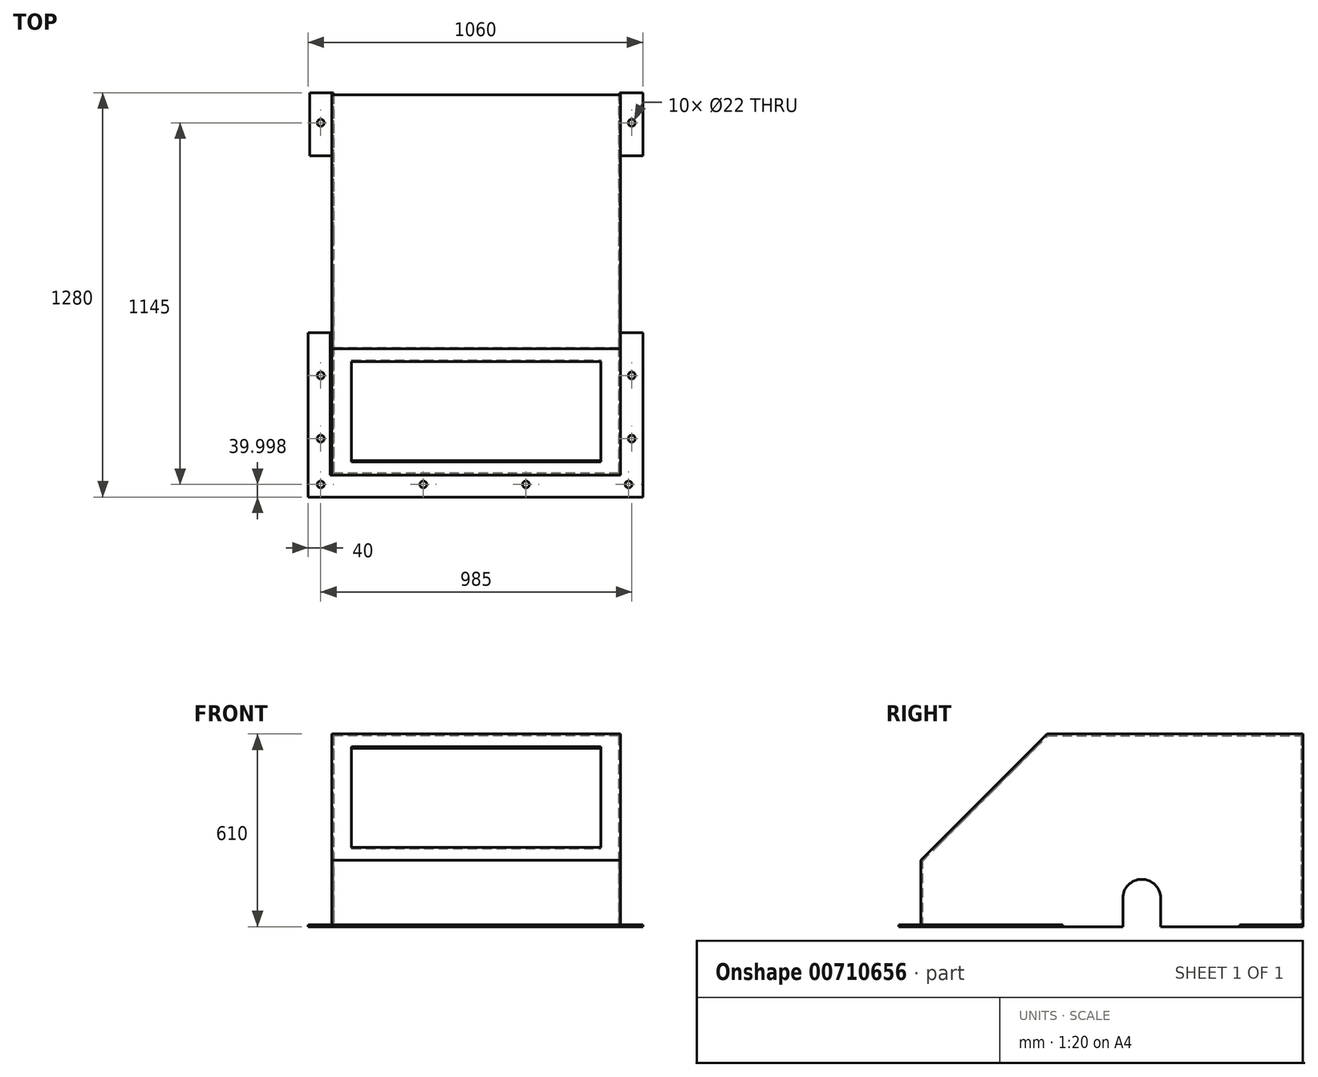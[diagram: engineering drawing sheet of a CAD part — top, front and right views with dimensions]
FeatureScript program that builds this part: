
annotation { "Feature Type Name" : "Feature", "Feature Type Description" : "" }
export const myFeature = defineFeature(function(context is Context, id is Id, definition is map)
    precondition{}
    {
        {
            var Q0;
            Q0=qCreatedBy(makeId("Right.planeOp"),FACE);
            var sketch = newSketch(context, id + "F0", { "sketchPlane" : qUnion([Q0])});
            skLineSegment(sketch, "E0", {"start": v(1114.84, 0) * mm, "end": v(-95.16, 0) * mm});
            skLineSegment(sketch, "E1", {"start": v(-95.16, 0) * mm, "end": v(-95.16, 210) * mm});
            skLineSegment(sketch, "E2", {"start": v(-95.16, 210) * mm, "end": v(304.84, 610) * mm});
            skLineSegment(sketch, "E3", {"start": v(304.84, 610) * mm, "end": v(1114.84, 610) * mm});
            skLineSegment(sketch, "E4", {"start": v(1114.84, 610) * mm, "end": v(1114.84, 0) * mm});
            skSolve(sketch);
        }
        {
            var Q0;
            Q0 = qSketchRegion(id + "F0", true);
            extrude(context, id + "F1", {"entities" : qUnion([Q0]), "endBound" : BoundingType.SYMMETRIC, "depth" : 915 * mm, "offsetDistance" : 25 * mm});
        }
        {
            var Q0;
            Q0=makeQuery(id+"F1.opExtrude","SWEPT_FACE",FACE,{"disambiguationData":[OSD([sQuery(id+"F0.wireOp",EDGE,"E0")])]});
            shell(context, id + "F2", {"entities" : qUnion([Q0]), "thickness" : 6 * mm});
        }
        {
            var Q0;
            Q0=makeQuery(id+"F1.opExtrude","SWEPT_FACE",FACE,{"disambiguationData":[OSD([sQuery(id+"F0.wireOp",EDGE,"E4")])]});
            var sketch = newSketch(context, id + "F3", { "sketchPlane" : qUnion([Q0])});
            skLineSegment(sketch, "E5.bottom", {"start": v(452.76, 610) * mm, "end": v(-454, 610) * mm});
            skLineSegment(sketch, "E5.left", {"start": v(452.76, 610) * mm, "end": v(454, 0) * mm});
            skPoint(sketch, "E5.middle", {"position": v(0, 305) * mm});
            skPoint(sketch, "E5.middle.positionSnap0", {"position": v(457.5, 305) * mm});
            skPoint(sketch, "E5.centerSnap0", {"position": v(457.5, 305) * mm});
            skLineSegment(sketch, "E6", {"start": v(-454, 610) * mm, "end": v(-454, 0) * mm});
            skLineSegment(sketch, "E7", {"start": v(-454, 0) * mm, "end": v(454, 0) * mm});
            skSolve(sketch);
        }
        {
            var Q0;
            Q0 = qSketchRegion(id + "F3", true);
            extrude(context, id + "F4", {"entities" : qUnion([Q0]), "operationType" : NewBodyOperationType.REMOVE, "oppositeDirection" : true, "depth" : 6 * mm, "offsetDistance" : 25 * mm});
        }
        {
            var Q0;
            Q0=makeQuery(id+"F1.opExtrude","SWEPT_FACE",FACE,{"disambiguationData":[OSD([sQuery(id+"F0.wireOp",EDGE,"E0")])]});
            var sketch = newSketch(context, id + "F5", { "sketchPlane" : qUnion([Q0])});
            skLineSegment(sketch, "E8.top", {"start": v(-462.5, -354.84) * mm, "end": v(-532.5, -354.84) * mm});
            skLineSegment(sketch, "E8.left", {"start": v(-462.5, 95.16) * mm, "end": v(-462.5, -354.84) * mm});
            skLineSegment(sketch, "E9", {"start": v(-532.5, 165.16) * mm, "end": v(-532.5, -354.84) * mm});
            skLineSegment(sketch, "E10", {"start": v(527.5, 165.16) * mm, "end": v(527.5, -354.84) * mm});
            skLineSegment(sketch, "E11", {"start": v(527.5, -354.84) * mm, "end": v(457.5, -354.84) * mm});
            skLineSegment(sketch, "E12", {"start": v(457.5, -354.84) * mm, "end": v(457.5, 95.16) * mm});
            skLineSegment(sketch, "E13", {"start": v(457.5, 95.16) * mm, "end": v(-462.5, 95.16) * mm});
            skLineSegment(sketch, "E14", {"start": v(-532.5, 165.16) * mm, "end": v(527.5, 165.16) * mm});
            skLineSegment(sketch, "E15", {"start": v(-457.5, -1114.84) * mm, "end": v(-527.5, -1114.84) * mm});
            skLineSegment(sketch, "E16", {"start": v(-527.5, -1114.84) * mm, "end": v(-527.5, -914.84) * mm});
            skLineSegment(sketch, "E17", {"start": v(-527.5, -914.84) * mm, "end": v(-457.5, -914.84) * mm});
            skLineSegment(sketch, "E18", {"start": v(-457.5, -914.84) * mm, "end": v(-457.5, -1114.84) * mm});
            skCircle(sketch, "E19", {"center": v(-492.5, 125.16) * mm, "radius": 11 * mm});
            skCircle(sketch, "E20", {"center": v(-167.5, 125.16) * mm, "radius": 11 * mm});
            skCircle(sketch, "E21", {"center": v(157.5, 125.16) * mm, "radius": 11 * mm});
            skCircle(sketch, "E22", {"center": v(482.5, 125.16) * mm, "radius": 11 * mm});
            skCircle(sketch, "E23", {"center": v(-492.5, -19.84) * mm, "radius": 11 * mm});
            skCircle(sketch, "E24", {"center": v(-492.5, -219.84) * mm, "radius": 11 * mm});
            skCircle(sketch, "E25", {"center": v(-492.5, -1019.84) * mm, "radius": 11 * mm});
            skCircle(sketch, "E26.MirrorC", {"center": v(492.5, -1019.84) * mm, "radius": 11 * mm});
            skLineSegment(sketch, "E27.MirrorCS", {"start": v(527.5, -1114.84) * mm, "end": v(527.5, -914.84) * mm});
            skLineSegment(sketch, "E28.MirrorCS", {"start": v(457.5, -914.84) * mm, "end": v(457.5, -1114.84) * mm});
            skLineSegment(sketch, "E29.MirrorCS", {"start": v(527.5, -914.84) * mm, "end": v(457.5, -914.84) * mm});
            skLineSegment(sketch, "E30.MirrorCS", {"start": v(457.5, -1114.84) * mm, "end": v(527.5, -1114.84) * mm});
            skCircle(sketch, "E31.MirrorC", {"center": v(492.5, -219.84) * mm, "radius": 11 * mm});
            skCircle(sketch, "E32.MirrorC", {"center": v(492.5, -19.84) * mm, "radius": 11 * mm});
            skSolve(sketch);
        }
        {
            var Q0;
            Q0 = qSketchRegion(id + "F5", true);
            extrude(context, id + "F6", {"entities" : qUnion([Q0]), "oppositeDirection" : true, "depth" : 6 * mm, "offsetDistance" : 25 * mm});
        }
        {
            var Q0;
            Q0=makeQuery(id+"F1.opExtrude","CAP_FACE",FACE,{"disambiguationData":[OSD([sQuery(id+"F0.wireOp",EDGE,"E0"),sQuery(id+"F0.wireOp",EDGE,"E1"),sQuery(id+"F0.wireOp",EDGE,"E2"),sQuery(id+"F0.wireOp",EDGE,"E3"),sQuery(id+"F0.wireOp",EDGE,"E4")])],"isStart":true});
            var sketch = newSketch(context, id + "F7", { "sketchPlane" : qUnion([Q0])});
            skLineSegment(sketch, "E33", {"start": v(-664.84, 0) * mm, "end": v(-664.84, 90) * mm});
            skLineSegment(sketch, "E34", {"start": v(-664.84, 0) * mm, "end": v(-544.84, 0) * mm});
            skLineSegment(sketch, "E35", {"start": v(-544.84, 0) * mm, "end": v(-544.84, 90) * mm});
            skArc(sketch, "E36", {"start": v(-544.84, 90) * mm, "mid": v(-604.84, 150) * mm, "end": v(-664.84, 90) * mm});
            skSolve(sketch);
        }
        {
            var Q0;
            Q0 = qSketchRegion(id + "F7", true);
            extrude(context, id + "F8", {"entities" : qUnion([Q0]), "operationType" : NewBodyOperationType.REMOVE, "endBound" : BoundingType.THROUGH_ALL, "oppositeDirection" : true, "depth" : 25 * mm, "offsetDistance" : 25 * mm});
        }
        {
            var Q0;
            Q0=makeQuery(id+"F1.opExtrude","SWEPT_FACE",FACE,{"disambiguationData":[OSD([sQuery(id+"F0.wireOp",EDGE,"E2")])]});
            var sketch = newSketch(context, id + "F9", { "sketchPlane" : qUnion([Q0])});
            skLineSegment(sketch, "E37.bottom", {"start": v(-395, 589.39) * mm, "end": v(395, 589.39) * mm});
            skLineSegment(sketch, "E37.top", {"start": v(-395, 139.39) * mm, "end": v(395, 139.39) * mm});
            skLineSegment(sketch, "E37.left", {"start": v(-395, 589.39) * mm, "end": v(-395, 139.39) * mm});
            skLineSegment(sketch, "E37.right", {"start": v(395, 589.39) * mm, "end": v(395, 139.39) * mm});
            skSolve(sketch);
        }
        {
            var Q0;
            Q0 = qSketchRegion(id + "F9", true);
            extrude(context, id + "F10", {"entities" : qUnion([Q0]), "operationType" : NewBodyOperationType.REMOVE, "oppositeDirection" : true, "depth" : 6 * mm, "offsetDistance" : 25 * mm});
        }
    });
